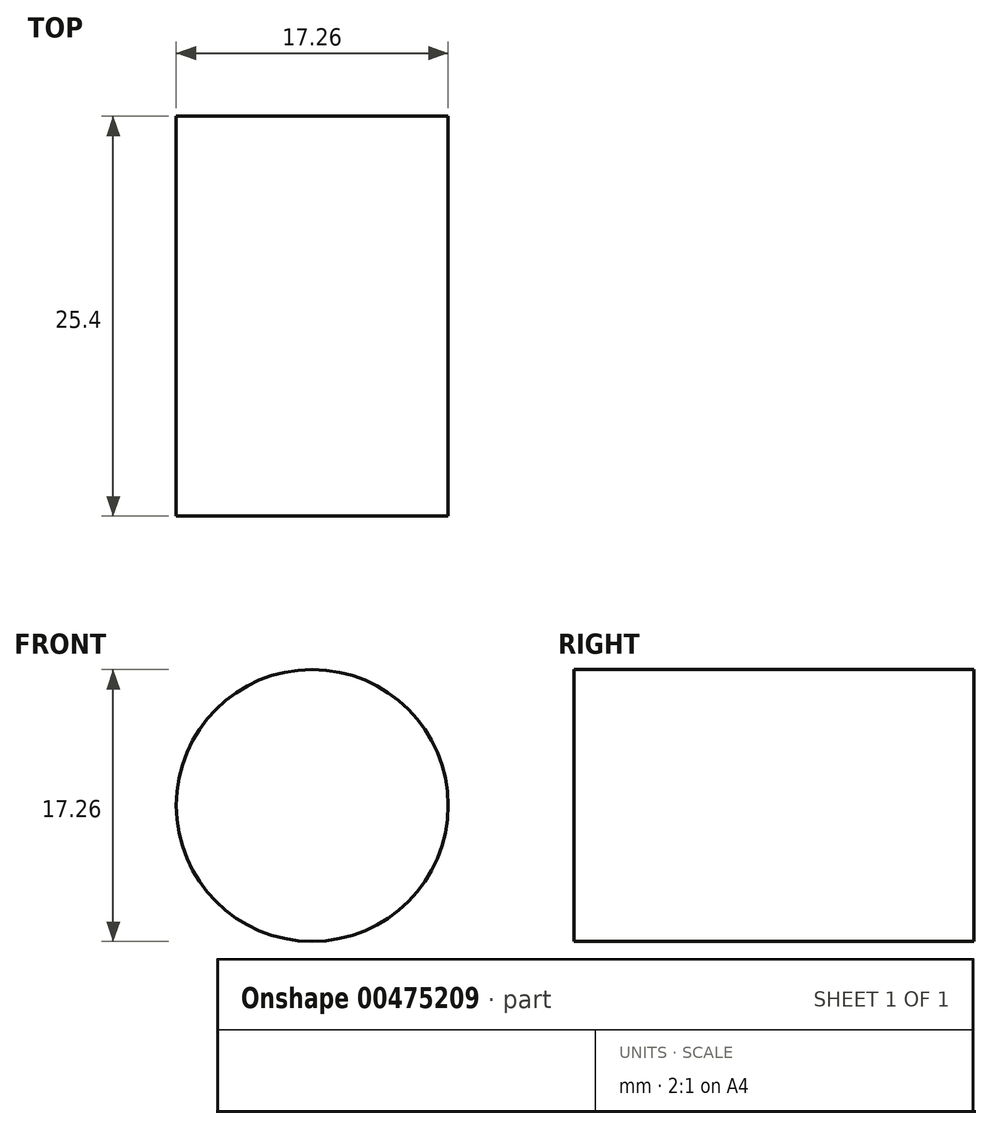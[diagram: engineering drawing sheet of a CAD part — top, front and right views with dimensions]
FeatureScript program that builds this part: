
annotation { "Feature Type Name" : "Feature", "Feature Type Description" : "" }
export const myFeature = defineFeature(function(context is Context, id is Id, definition is map)
    precondition{}
    {
        {
            var Q0;
            Q0=qCreatedBy(makeId("Front.planeOp"),FACE);
            var sketch = newSketch(context, id + "F0", { "sketchPlane" : qUnion([Q0])});
            skCircle(sketch, "E0", {"center": v(0, 0) * mm, "radius": 8.63 * mm});
            skLineSegment(sketch, "E1", {"start": v(0, 0) * mm, "end": v(0, 57.27) * mm});
            skLineSegment(sketch, "E2", {"start": v(0, 0) * mm, "end": v(44.46, 0) * mm});
            skLineSegment(sketch, "E3", {"start": v(0, 17.33) * mm, "end": v(0, 57.27) * mm});
            skLineSegment(sketch, "E4", {"start": v(0, 17.33) * mm, "end": v(0, 0) * mm});
            skSolve(sketch);
        }
        {
            var Q0;
            Q0 = qSketchRegion(id + "F0", true);
            extrude(context, id + "F1", {"entities" : qUnion([Q0]), "depth" : 25.4 * mm});
        }
    });
